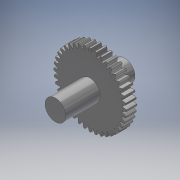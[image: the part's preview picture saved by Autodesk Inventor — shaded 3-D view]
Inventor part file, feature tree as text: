
AUTODESK INVENTOR PART (.ipt)
format: ipt  version: 2019 (Build 230136000, 136)  size: 309,760 bytes
history: native  units: mm (DEFAULTED — no unit token found)
features: plane x3, other x3, sketch x3, extrude x2
ambient origin geometry x8: Origin, YZ Plane, XZ Plane, XY Plane, X Axis, Y Axis, Z Axis, Center Point
bodies: Solid1 (feature_tree)
feature tree (11):
  extrude  "Extrusion1"  Depth=3.0mm TaperAngle=0.0deg
  plane  "Work Plane2"
  plane  "Work Plane8"
  plane  "Work Plane9"
  other  "Przekładnia walcowa"
  extrude  "Wyciągnięcie proste2"  Depth=10.0mm TaperAngle=0.0deg
  sketch  "Sketch1"  dims[d0=21.0mm d1=3.0mm d2=0.0mm]
  sketch  "Sketch2"  dims[d3=20.0mm d4=10.0mm d5=0.0mm d16=13.75mm d17=0.0mm d34=0.785398mm d39=0.0mm d41=0.0mm d43=13.75mm d46=13.75mm d47=0.0mm d48=0.0mm d49=6.0mm d50=10.0mm d51=10.0mm d52=0.0mm d53=0.0mm]
  other  "Srf1"
  sketch  "Szkic3"
  other  "Średnica podziałowa"
